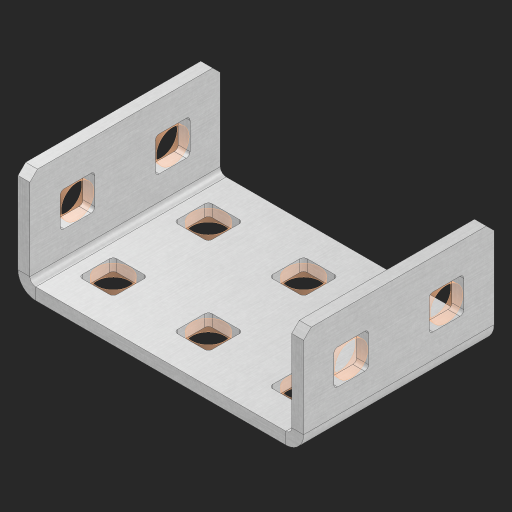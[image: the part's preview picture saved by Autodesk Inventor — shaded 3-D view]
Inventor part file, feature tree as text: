
AUTODESK INVENTOR PART (.ipt)
format: ipt  version: 2023 (Build 270158000, 158)  size: 544,256 bytes
history: native  units: in
note: dims shown in document units (in); Inventor stores cm internally (conversion verified against a paired STEP export)
features: other x15, sheet_metal_op x10, extrude x9, sketch x8, mirror x1, pattern_linear x1, chamfer x1
ambient origin geometry x8: Origin, YZ Plane, XZ Plane, XY Plane, X Axis, Y Axis, Z Axis, Center Point
bodies: Solid1 (feature_tree), Body (feature_tree)
feature tree (45):
  other  "Flange Pattern Plane"
  sheet_metal_op  "Flange Pattern"
  sheet_metal_op  "Body Pattern"
  other  "Arc Length"
  mirror  "Notch Mirror"
  pattern_linear  "Notch Pattern"  Spacing1=0.25in  [1 undecoded]
  chamfer  "End Chamfer"
  extrude  "Half Cut"  Depth=0.0625in
  sketch  "Sketch1"  dims[d0=1.5in]
  other  "Plate1"
  sketch  "Sketch2"  dims[d1=1.0in]
  other  "Plate2"
  sheet_metal_op  "Bend1"
  sheet_metal_op  "Corner1"
  sketch  "Sketch3"  dims[d2=0.0625in]
  other  "Flange Pattern Sketch"
  sketch  "Sketch7"  dims[d3=0.0625in]
  other  "Srf1"
  other  "Srf2"
  sketch  "Sketch8"  dims[d4=0.0312in]
  sketch  "Sketch9"  dims[d5=0.125in]
  other  "Srf91"
  sheet_metal_op  "Body Pattern Sketch"
  other  "Srf92"
  sketch  "Sketch13"  dims[d6=0.0625in]
  sketch  "Sketch14"  dims[d7=0.5in d8=90.0deg d9=0.0312in d10=0.25in d11=0.0625in d12=0.0625in d16=0.182in d17=0.02in d18=0.0625in d19=0.0in d20=0.25in d21=0.25in d46=0.172in d47=1.0in d48=0.0in d49=0.182in d50=0.02in d51=0.25in d52=0.25in d53=0.0625in d54=0.0in d55=0.172in d56=1.0in d57=0.0in d60=0.7874in d62=0.5in d63=1.1811in d65=0.5in d85=0.1473in d86=0.1782in d88=0.04in d89=0.0625in d90=0.0in d91=0.04in d92=0.0491in d95=2.5in d96=0.04in d97=0.25in d98=45.0deg d101=0.0in d102=2.497in d131=1.5in d132=0.7874in d134=0.5in d139=0.5in]
  other  "Srf856"
  other  "Srf1310"
  other  "Srf1311"
  other  "Srf1376"
  other  "Srf1377"
  other  "Srf1755"
  sheet_metal_op  "Flange Stamp"
  sheet_metal_op  "Flange Circle"
  sheet_metal_op  "Body Stamp"
  sheet_metal_op  "Body Circle"
  sheet_metal_op  "Notch"
  extrude  "ExtrusionSrf2"  Depth=0.0625in
  extrude  "ExtrusionSrf92"  Depth=0.182in
  extrude  "ExtrusionSrf856"  Depth=0.02in
  extrude  "ExtrusionSrf1310"  Depth=0.0625in
  extrude  "ExtrusionSrf1311"  TaperAngle=0.0deg  [1 undecoded]
  extrude  "ExtrusionSrf1376"  Depth=0.25in
  extrude  "ExtrusionSrf1377"  Depth=0.25in
  extrude  "ExtrusionSrf1755"  Depth=0.5in
note: 2 required parameter values undecoded (feature->parameter linkage not recoverable at this tier; creation-order binding heuristic only, values carry confidence <= 0.55)
